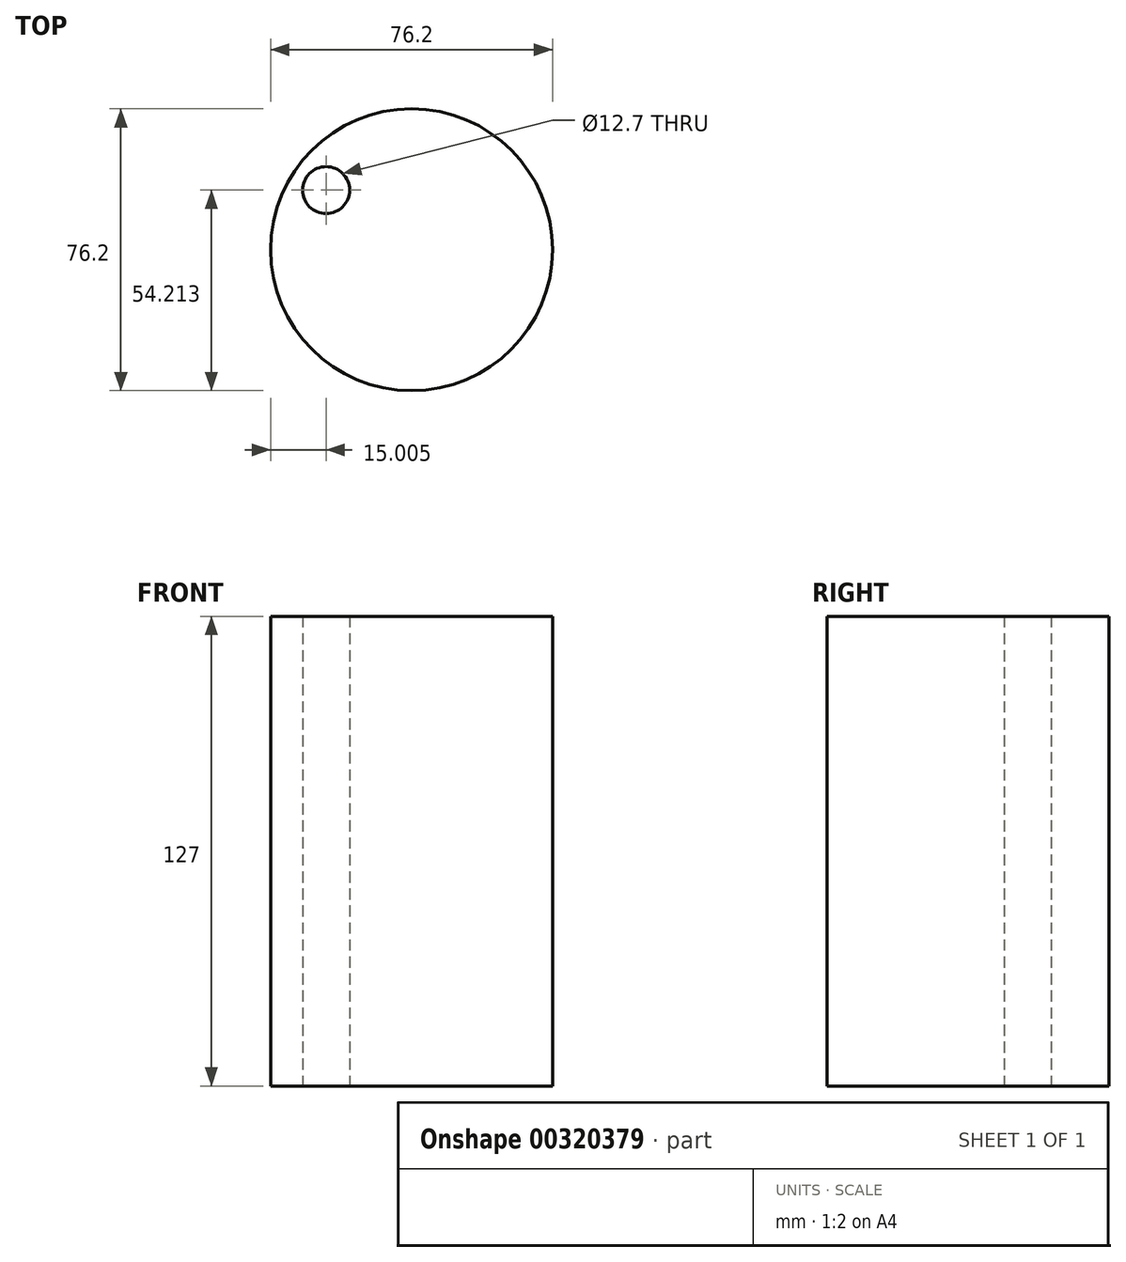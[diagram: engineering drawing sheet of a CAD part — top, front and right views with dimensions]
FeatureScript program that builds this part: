
annotation { "Feature Type Name" : "Feature", "Feature Type Description" : "" }
export const myFeature = defineFeature(function(context is Context, id is Id, definition is map)
    precondition{}
    {
        {
            var Q0;
            Q0=qCreatedBy(makeId("Top.planeOp"),FACE);
            var sketch = newSketch(context, id + "F0", { "sketchPlane" : qUnion([Q0])});
            skCircle(sketch, "E0", {"center": v(0, 0) * mm, "radius": 38.1 * mm});
            skCircle(sketch, "E1", {"center": v(-23.1, 16.11) * mm, "radius": 6.35 * mm});
            skSolve(sketch);
        }
        {
            var Q0;
            Q0=makeQuery(id+"F0.imprint","IMPRINT",FACE,{"disambiguationData":[TD([[makeQuery(id+"F0.imprint","IMPRINT",EDGE,{"derivedFrom":sQuery(id+"F0.wireOp",EDGE,"E0")}),1.0]])]});
            extrude(context, id + "F1", {"entities" : qUnion([Q0]), "depth" : 127 * mm});
        }
    });
